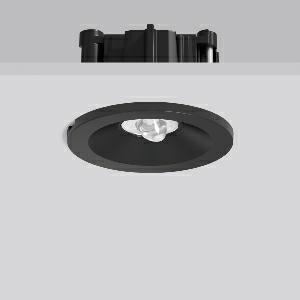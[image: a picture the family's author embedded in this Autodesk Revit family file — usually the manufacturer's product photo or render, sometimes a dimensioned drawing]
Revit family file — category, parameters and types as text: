
# Revit family: turia_l_672562_003_89_6b42
name_source: partatom
category: Lighting Fixtures
units: mm (PartAtom-declared; Revit-internal decimal feet)

## family parameters
Cut with Voids When Loaded = No
Host = Face
Light Source = No
Part Type = Normal
Room Calculation Point = No
Round Connector Dimension = Use Diameter
Shared = No

## types (1)
- TURIA L (1 x LED Modul 765, 220 lm, 6500)
    Apparent Load = 5 VA
    CIE Flux Codes = 70 91 99 100 100
    Color Rendering = 70
    Color Temperature = 6500
    Default Elevation = 1800 mm
    Description = Series: TURIA L
Round emergency luminaire for escape route lighting. With asymmetrical beam plastic lenses for illuminating rescue facilities. Suitable for connection to central battery systems. With MOM monitoring module for LPS (Low Power Supply) small central battery units of the type Easy+IP. With enclosed separate ceiling mounting ring also suitable for ceiling cut-outs of Ø 68 mm. 
Colour: black
Diameter: 62 mm
Height: 3 mm
Cut-out diameter: 54-68 mm
Recess height: 76-162 mm
Luminaire: recess height: 42 mm
Weight: 350 g
Operating mode: non-maintained power mode
Lamp: LED
Socket: without socket
Colour temperature: 6500K
Colour rendering index (CRI): 70
System power: 4.8 W
Rated luminous flux: 220 lm
Luminous flux, emergency: 220 lm
System power, emergency: 4.8 W
Control gear: Regulated power supply
Protection class: II
Type of protection: IP 20
    Height = 0 mm  [stored 0 ft]
    Lamp = 1 x LED Modul 765
    Lamp Light Flux = 220 lm
    Lamp count = 1
    Length = 62 mm  [stored 0.203412 ft]
    Lifetime = 50000 h
    Luminous efficacy = 46 lm/W
    Manufacturer = RZB
    ModVariant = No
    Model = 672562.003.89
    Mounting Place = Ceiling
    Mounting Type = Recessed
    Number of Poles = 1
    OnlyDefault = Yes
    Power Factor = 1
    Product Name = TURIA L
    Product group = Recessed ceiling luminaires
    ProductGroupID = 405
    Protection Class = Protection class II
    Protection Degree = IP 20
    RLX_Detail_Level = 1
    RLX_Emergency_Light_Flux = 220 lm
    RLX_Emergency_Type = 3
    RLX_Emergency_Type_DB = Yes
    RlxData = <blob elided: 58173 chars, md5=265b4d82>
    Socket = socket
    Standby Power = 0 W
    System Light Flux = 220 lm
    System Power = 5 W
    Type Comments = Product without accessories
    Type Image = 672561.003.jpg
    URL = http://relux.com
    VarID = ---
    Voltage = 230 V
    Voltage Range = 220-240 V
    Weight = 0.00 kg
    Width = 0 mm  [stored 0 ft]

note: [stored X ft] marks values corroborated as IEEE doubles in the binary element streams (Revit-internal decimal feet)

## geometry (parser evidence)
native form markers: Blend x4, Sweep x12
no freeform markers — native parametric forms only
